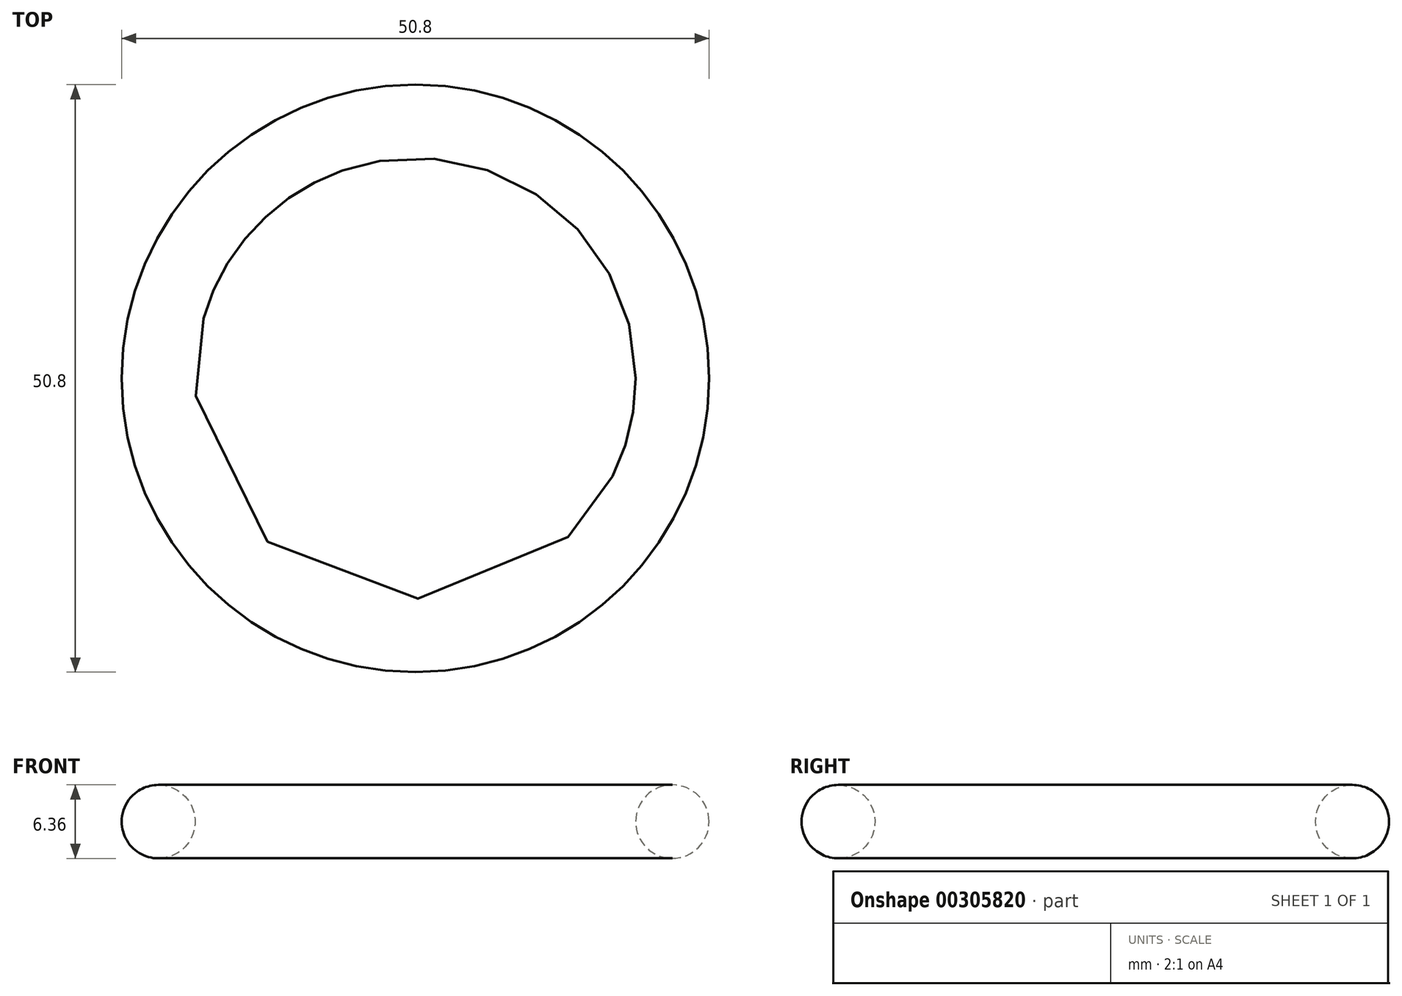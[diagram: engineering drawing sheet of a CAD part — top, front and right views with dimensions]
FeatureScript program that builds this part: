
annotation { "Feature Type Name" : "Feature", "Feature Type Description" : "" }
export const myFeature = defineFeature(function(context is Context, id is Id, definition is map)
    precondition{}
    {
        {
            var Q0;
            Q0=qCreatedBy(makeId("Front.planeOp"),FACE);
            var sketch = newSketch(context, id + "F0", { "sketchPlane" : qUnion([Q0])});
            skCircle(sketch, "E0", {"center": v(-22.22, 0) * mm, "radius": 3.18 * mm});
            skLineSegment(sketch, "E1", {"start": v(0, 43.13) * mm, "end": v(0, -16.86) * mm, "construction": true});
            skSolve(sketch);
        }
        {
            var Q0;
            Q0 = qSketchRegion(id + "F0", true);
            var Q1;
            Q1=sQuery(id+"F0.wireOp",EDGE,"E1");
            revolve(context, id + "F1", {"entities" : qUnion([Q0]), "axis" : qUnion([Q1]), "revolveType" : RevolveType.FULL});
        }
    });
